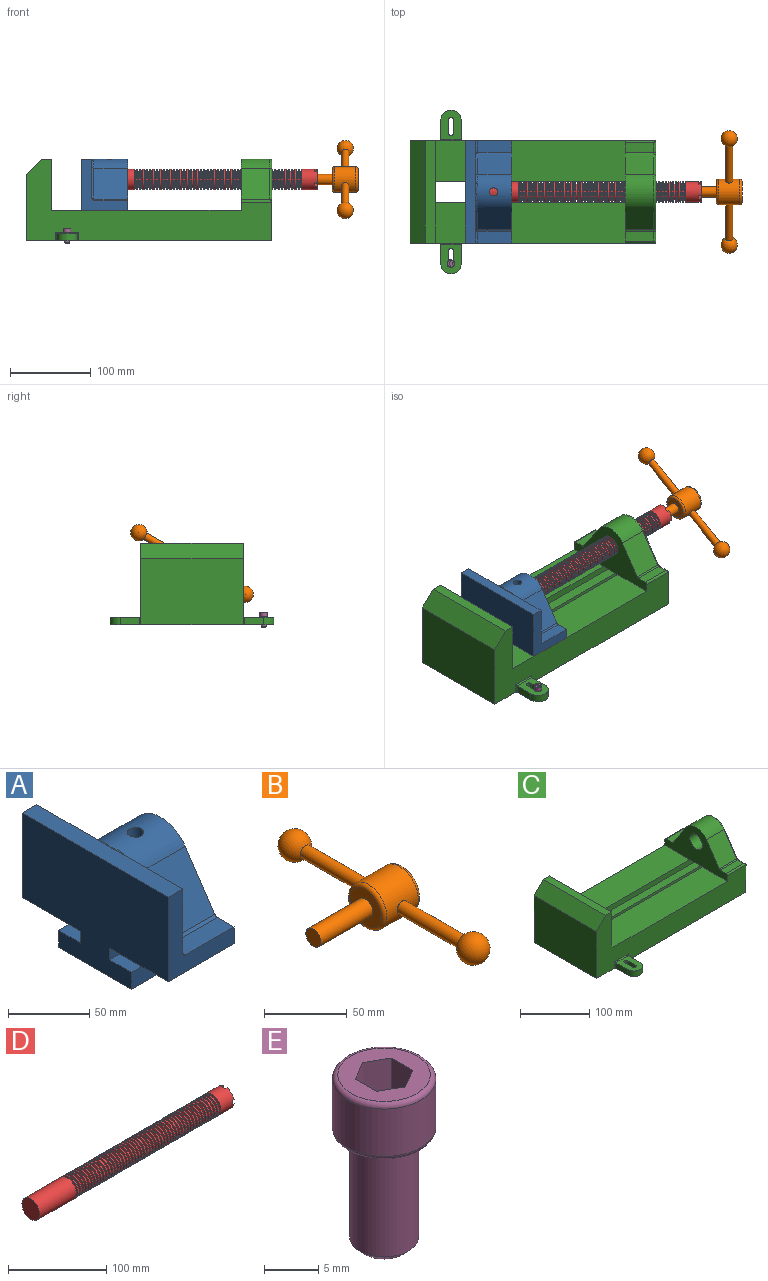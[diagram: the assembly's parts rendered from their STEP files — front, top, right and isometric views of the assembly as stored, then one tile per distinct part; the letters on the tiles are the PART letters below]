
ASSEMBLY  parts=5 mates=5
PART A: 36 faces, bbox 57.2x127x89 mm
  f0: plane 57.15x50.8mm, normal (0,0,-1), area 2903.2mm2, adj f6,f9,f10,f23
  f1: cylinder r=12.7mm len=44.45mm, axis (1,0,0), area 3464.3mm2, adj f6,f15,f16
  f2: plane 41.91x14.52mm, normal (0,0,1), area 608.5mm2, adj f6,f11,f24,f25
  f3: plane 51.86x48.26mm, normal (1,0,0), area 1495.7mm2, adj f8,f10,f31,f33,f35
  f4: plane 51.86x48.26mm, normal (1,0,0), area 1495.7mm2, adj f8,f11,f24,f28,f29
  f5: plane 57.15x50.8mm, normal (0,0,-1), area 2903.2mm2, adj f6,f9,f11,f22
  f6: plane 127x85.09mm, normal (1,0,0), area 5190.6mm2, adj f0,f1,f2,f5,f7,f10,f11,f12
  f7: plane 41.91x14.52mm, normal (0,0,1), area 608.5mm2, adj f6,f10,f30,f31
  f8: plane 127x12.7mm, normal (0,0,1), area 1612.9mm2, adj f3,f4,f9,f10,f11,f26,f34
  f9: plane 127x85.09mm, normal (-1,0,0), area 9096.8mm2, adj f0,f5,f8,f10,f11,f17,f18,f19
  f10: plane 63.5x57.15mm, normal (0,-1,0), area 1372.3mm2, adj f0,f3,f6,f7,f8,f9,f31
  f11: plane 63.5x57.15mm, normal (0,1,0), area 1372.3mm2, adj f2,f4,f5,f6,f8,f9,f24
  f12: plane 41.91x38.43mm, normal (0,-0.83,0.56), area 1939.2mm2, adj f6,f13,f30,f33
  f13: cylinder r=25.4mm len=44.45mm, axis (1,0,0), area 2026.5mm2, adj f6,f12,f14,f16,f26,f28,f34,f35
  f14: plane 41.91x38.43mm, normal (0,0.83,0.56), area 1939.2mm2, adj f6,f13,f25,f29
  f15: plane 25.4x25.4mm, normal (1,0,0), area 506.7mm2, adj f1
  f16: cylinder r=5.08mm len=13.76mm, axis (0,0,1), area 414mm2, adj f1,f13
  f17: plane 57.15x19.05mm, normal (0,0,1), area 1088.7mm2, adj f6,f9,f18,f23
  f18: plane 57.15x12.7mm, normal (0,-1,0), area 725.8mm2, adj f6,f9,f17,f19
  f19: plane 63.5x57.15mm, normal (0,0,-1), area 3629mm2, adj f6,f9,f18,f20
  f20: plane 57.15x12.7mm, normal (0,1,0), area 725.8mm2, adj f6,f9,f19,f21
  f21: plane 57.15x19.05mm, normal (0,0,1), area 1088.7mm2, adj f6,f9,f20,f22
  f22: plane 57.15x8.89mm, normal (0,1,0), area 508.1mm2, adj f5,f6,f9,f21
  f23: plane 57.15x8.89mm, normal (0,-1,0), area 508.1mm2, adj f0,f6,f9,f17
  f24: cylinder r=2.54mm len=14.52mm, axis (0,-1,0), area 57.9mm2, adj f2,f4,f11,f27
  f25: cylinder r=2.54mm len=41.91mm, axis (1,0,0), area 104.3mm2, adj f2,f6,f14,f27
  f26: bspline ~12.24x2.8mm, area 20.9mm2, adj f8,f13,f28
  f27: sphere r=2.54mm, area 6.3mm2, adj f24,f25,f29
  f28: torus R=27.94mm, axis (1,0,0), area 57.8mm2, adj f4,f13,f26,f29
  f29: cylinder r=2.54mm len=39.84mm, axis (0,-0.56,0.83), area 184.6mm2, adj f4,f14,f27,f28
  f30: cylinder r=2.54mm len=41.91mm, axis (1,0,0), area 104.3mm2, adj f6,f7,f12,f32
  f31: cylinder r=2.54mm len=14.52mm, axis (0,-1,0), area 57.9mm2, adj f3,f7,f10,f32
  f32: sphere r=2.54mm, area 6.3mm2, adj f30,f31,f33
  f33: cylinder r=2.54mm len=39.84mm, axis (0,-0.56,-0.83), area 184.6mm2, adj f3,f12,f32,f35
  f34: bspline ~12.24x2.8mm, area 20.9mm2, adj f8,f13,f35
  f35: torus R=27.94mm, axis (1,0,0), area 57.8mm2, adj f3,f13,f33,f34
PART B: 11 faces, bbox 76.2x172.7x34.4 mm
  f0: sphere r=10.16mm, area 1231.8mm2, adj f1
  f1: cylinder r=4.45mm len=51.82mm, axis (0,1,0), area 1438.5mm2, adj f0,f4
  f2: sphere r=10.16mm, area 1231.8mm2, adj f3
  f3: cylinder r=4.45mm len=51.82mm, axis (0,1,0), area 1438.5mm2, adj f2,f4
  f4: cylinder r=15.88mm len=31.75mm, axis (-1,0,0), area 2534.7mm2, adj f1,f3,f9,f10
  f5: cylinder r=6.35mm len=44.45mm, axis (-1,0,0), area 1773.5mm2, adj f6,f8
  f6: plane 12.7x12.7mm, normal (-1,0,0), area 126.7mm2, adj f5
  f7: plane 26.67x26.67mm, normal (1,0,0), area 558.6mm2, adj f10
  f8: plane 26.67x26.67mm, normal (-1,0,0), area 432mm2, adj f5,f9
  f9: torus R=13.33mm, axis (1,0,0), area 374.8mm2, adj f4,f8
  f10: torus R=13.33mm, axis (1,0,0), area 374.8mm2, adj f4,f7
PART C: 61 faces, bbox 304.8x203.2x103.7 mm
  f0: plane 304.8x101.6mm, normal (0,1,0), area 13520.3mm2, adj f3,f4,f5,f6,f7,f8,f9,f16
  f1: plane 304.8x101.6mm, normal (0,-1,0), area 13520.3mm2, adj f2,f3,f5,f6,f7,f8,f9,f16
  f2: plane 234.95x50.8mm, normal (0,0,1), area 11935.5mm2, adj f1,f5,f16,f26
  f3: plane 127x99.06mm, normal (1,0,0), area 7097.5mm2, adj f0,f1,f9,f14,f17,f18,f19,f20
  f4: plane 234.95x50.8mm, normal (0,0,1), area 11935.5mm2, adj f0,f5,f16,f27
  f5: plane 127x101.6mm, normal (1,0,0), area 9516.1mm2, adj f0,f1,f2,f4,f6,f9,f18,f19
  f6: plane 127x12.7mm, normal (0,0,1), area 1612.9mm2, adj f0,f1,f5,f7
  f7: plane 127x19.05mm, normal (-0.71,0,0.71), area 3421.5mm2, adj f0,f1,f6,f8
  f8: plane 127x82.55mm, normal (-1,0,0), area 10483.8mm2, adj f0,f1,f7,f9
  f9: plane 304.8x203.2mm, normal (0,0,-1), area 33298.3mm2, adj f0,f1,f3,f5,f8,f21,f22,f39
  f10: plane 35.56x11.98mm, normal (0,0,1), area 426mm2, adj f16,f28,f29,f30
  f11: plane 38.43x35.56mm, normal (0,0.83,0.56), area 1645.4mm2, adj f12,f16,f29,f32
  f12: cylinder r=25.4mm len=42.19mm, axis (1,0,0), area 1770.2mm2, adj f11,f13,f16,f33
  f13: plane 38.43x35.56mm, normal (0,-0.83,0.56), area 1645.4mm2, adj f12,f16,f34,f35
  f14: cylinder r=12.7mm len=38.1mm, axis (1,0,0), area 3040.2mm2, adj f3,f16
  f15: plane 35.56x11.98mm, normal (0,0,1), area 426mm2, adj f16,f34,f36,f38
  f16: plane 127x63.5mm, normal (-1,0,0), area 4155.5mm2, adj f0,f1,f2,f4,f10,f11,f12,f13
  f17: plane 38.1x25.4mm, normal (0,0,-1), area 967.7mm2, adj f3,f16,f26,f27
  f18: plane 273.05x19.05mm, normal (0,0,-1), area 5201.6mm2, adj f3,f5,f19,f26
  f19: plane 273.05x12.7mm, normal (0,1,0), area 3467.7mm2, adj f3,f5,f18,f20
  f20: plane 273.05x19.05mm, normal (0,0,1), area 5201.6mm2, adj f3,f5,f19,f21
  f21: plane 273.05x16.51mm, normal (0,1,0), area 4508.1mm2, adj f3,f5,f9,f20
  f22: plane 273.05x16.51mm, normal (0,-1,0), area 4508.1mm2, adj f3,f5,f9,f23
  f23: plane 273.05x19.05mm, normal (0,0,1), area 5201.6mm2, adj f3,f5,f22,f24
  f24: plane 273.05x12.7mm, normal (0,-1,0), area 3467.7mm2, adj f3,f5,f23,f25
  f25: plane 273.05x19.05mm, normal (0,0,-1), area 5201.6mm2, adj f3,f5,f24,f27
  f26: plane 273.05x8.89mm, normal (0,1,0), area 2427.4mm2, adj f2,f3,f5,f17,f18
  f27: plane 273.05x8.89mm, normal (0,-1,0), area 2427.4mm2, adj f3,f4,f5,f17,f25
  f28: cylinder r=2.54mm len=38.1mm, axis (1,0,0), area 148.3mm2, adj f0,f10,f16,f30
  f29: cylinder r=2.54mm len=35.56mm, axis (-1,0,0), area 88.5mm2, adj f10,f11,f16,f31
  f30: cylinder r=2.54mm len=14.52mm, axis (0,1,0), area 54.3mm2, adj f3,f10,f28,f31
  f31: torus R=5.08mm, axis (-1,0,0), area 13.5mm2, adj f3,f29,f30,f32
  f32: cylinder r=2.54mm len=39.84mm, axis (0,0.56,-0.83), area 184.6mm2, adj f3,f11,f31,f33
  f33: torus R=22.86mm, axis (-1,0,0), area 191.4mm2, adj f3,f12,f32,f35
  f34: cylinder r=2.54mm len=35.56mm, axis (-1,0,0), area 88.5mm2, adj f13,f15,f16,f37
  f35: cylinder r=2.54mm len=39.84mm, axis (0,0.56,0.83), area 184.6mm2, adj f3,f13,f33,f37
  f36: cylinder r=2.54mm len=38.1mm, axis (-1,0,0), area 148.3mm2, adj f1,f15,f16,f38
  f37: torus R=5.08mm, axis (-1,0,0), area 13.5mm2, adj f3,f34,f35,f38
  f38: cylinder r=2.54mm len=14.52mm, axis (0,1,0), area 54.3mm2, adj f3,f15,f36,f37
  f39: plane 23.88x9.53mm, normal (-1,0,0), area 227.4mm2, adj f9,f45,f46,f60
  f40: plane 23.88x9.53mm, normal (1,0,0), area 227.4mm2, adj f9,f45,f46,f58
  f41: cylinder r=3.3mm len=9.53mm, axis (0,0,-1), area 98.8mm2, adj f9,f42,f44,f46
  f42: plane 15.62x9.53mm, normal (-1,0,0), area 148.8mm2, adj f9,f41,f43,f46
  f43: cylinder r=3.3mm len=9.53mm, axis (0,0,-1), area 98.8mm2, adj f9,f42,f44,f46
  f44: plane 15.62x9.53mm, normal (1,0,0), area 148.8mm2, adj f9,f41,f43,f46
  f45: cylinder r=12.7mm len=25.4mm, axis (0,0,-1), area 380mm2, adj f9,f39,f40,f46
  f46: plane 36.58x25.4mm, normal (0,0,1), area 722.4mm2, adj f39,f40,f41,f42,f43,f44,f45,f59
  f47: plane 23.88x9.53mm, normal (-1,0,0), area 227.4mm2, adj f9,f53,f54,f56
  f48: plane 23.88x9.53mm, normal (1,0,0), area 227.4mm2, adj f9,f53,f54,f55
  f49: cylinder r=3.3mm len=9.53mm, axis (0,0,-1), area 98.8mm2, adj f9,f50,f52,f54
  f50: plane 15.62x9.53mm, normal (-1,0,0), area 148.8mm2, adj f9,f49,f51,f54
  f51: cylinder r=3.3mm len=9.53mm, axis (0,0,-1), area 98.8mm2, adj f9,f50,f52,f54
  f52: plane 15.62x9.53mm, normal (1,0,0), area 148.8mm2, adj f9,f49,f51,f54
  f53: cylinder r=12.7mm len=25.4mm, axis (0,0,-1), area 380mm2, adj f9,f47,f48,f54
  f54: plane 36.58x25.4mm, normal (0,0,1), area 722.4mm2, adj f47,f48,f49,f50,f51,f52,f53,f57
  f55: cylinder r=1.52mm len=11.05mm, axis (0,0,-1), area 24.1mm2, adj f0,f9,f48,f57
  f56: cylinder r=1.52mm len=11.05mm, axis (0,0,1), area 24.1mm2, adj f0,f9,f47,f57
  f57: cylinder r=1.52mm len=28.45mm, axis (1,0,0), area 63.5mm2, adj f0,f54,f55,f56
  f58: cylinder r=1.52mm len=11.05mm, axis (0,0,1), area 24.1mm2, adj f1,f9,f40,f59
  f59: cylinder r=1.52mm len=28.45mm, axis (-1,0,0), area 63.5mm2, adj f1,f46,f58,f60
  f60: cylinder r=1.52mm len=11.05mm, axis (0,0,-1), area 24.1mm2, adj f1,f9,f39,f59
PART D: 220 faces, bbox 279.4x25.4x25.4 mm
  f0: cylinder r=12.7mm len=25.4mm, axis (-1,0,0), area 1468.2mm2, adj f1,f2,f3,f5,f7,f208,f209,f210
  f1: plane 9.9x9.9mm, normal (1,0,0), area 62.3mm2, adj f0,f4,f213,f216
  f2: plane 9.9x9.9mm, normal (1,0,0), area 62.3mm2, adj f0,f4,f210,f218
  f3: plane 9.9x9.9mm, normal (1,0,0), area 62.3mm2, adj f0,f4,f209,f212
  f4: cylinder r=6.35mm len=25.4mm, axis (1,0,0), area 960.3mm2, adj f1,f2,f3,f5,f6,f208,f209,f210
  f5: plane 9.9x9.9mm, normal (1,0,0), area 62.3mm2, adj f0,f4,f215,f217
  f6: plane 12.7x12.7mm, normal (1,0,0), area 126.7mm2, adj f4
  f7: cone r=12.7mm half-angle=76deg, axis (1,0,0), area 188mm2, adj f0,f9
  f8: cone r=10.16mm half-angle=76deg, axis (-1,0,0), area 188mm2, adj f9,f10
  f9: cylinder r=10.16mm len=20.32mm, axis (1,0,0), area 81.1mm2, adj f7,f8
  f10: cylinder r=12.7mm len=25.4mm, axis (-1,0,0), area 131.7mm2, adj f8,f11
  f11: cone r=12.7mm half-angle=76deg, axis (1,0,0), area 188mm2, adj f10,f13
  f12: cone r=10.16mm half-angle=76deg, axis (-1,0,0), area 188mm2, adj f13,f14
  f13: cylinder r=10.16mm len=20.32mm, axis (1,0,0), area 81.1mm2, adj f11,f12
  f14: cylinder r=12.7mm len=25.4mm, axis (-1,0,0), area 131.7mm2, adj f12,f15
  f15: cone r=12.7mm half-angle=76deg, axis (1,0,0), area 188mm2, adj f14,f17
  f16: cone r=10.16mm half-angle=76deg, axis (-1,0,0), area 188mm2, adj f17,f18
  f17: cylinder r=10.16mm len=20.32mm, axis (1,0,0), area 81.1mm2, adj f15,f16
  f18: cylinder r=12.7mm len=25.4mm, axis (-1,0,0), area 131.7mm2, adj f16,f19
  f19: cone r=12.7mm half-angle=76deg, axis (1,0,0), area 188mm2, adj f18,f21
  f20: cone r=10.16mm half-angle=76deg, axis (-1,0,0), area 188mm2, adj f21,f22
  f21: cylinder r=10.16mm len=20.32mm, axis (1,0,0), area 81.1mm2, adj f19,f20
  f22: cylinder r=12.7mm len=25.4mm, axis (-1,0,0), area 131.7mm2, adj f20,f23
  f23: cone r=12.7mm half-angle=76deg, axis (1,0,0), area 188mm2, adj f22,f25
  f24: cone r=10.16mm half-angle=76deg, axis (-1,0,0), area 188mm2, adj f25,f26
  f25: cylinder r=10.16mm len=20.32mm, axis (1,0,0), area 81.1mm2, adj f23,f24
  f26: cylinder r=12.7mm len=25.4mm, axis (-1,0,0), area 131.7mm2, adj f24,f27
  f27: cone r=12.7mm half-angle=76deg, axis (1,0,0), area 188mm2, adj f26,f29
  f28: cone r=10.16mm half-angle=76deg, axis (-1,0,0), area 188mm2, adj f29,f30
  f29: cylinder r=10.16mm len=20.32mm, axis (1,0,0), area 81.1mm2, adj f27,f28
  f30: cylinder r=12.7mm len=25.4mm, axis (-1,0,0), area 131.7mm2, adj f28,f31
  f31: cone r=12.7mm half-angle=76deg, axis (1,0,0), area 188mm2, adj f30,f33
  f32: cone r=10.16mm half-angle=76deg, axis (-1,0,0), area 188mm2, adj f33,f34
  f33: cylinder r=10.16mm len=20.32mm, axis (1,0,0), area 81.1mm2, adj f31,f32
  f34: cylinder r=12.7mm len=25.4mm, axis (-1,0,0), area 131.7mm2, adj f32,f35
  f35: cone r=12.7mm half-angle=76deg, axis (1,0,0), area 188mm2, adj f34,f37
  f36: cone r=10.16mm half-angle=76deg, axis (-1,0,0), area 188mm2, adj f37,f38
  f37: cylinder r=10.16mm len=20.32mm, axis (1,0,0), area 81.1mm2, adj f35,f36
  f38: cylinder r=12.7mm len=25.4mm, axis (-1,0,0), area 131.7mm2, adj f36,f39
  f39: cone r=12.7mm half-angle=76deg, axis (1,0,0), area 188mm2, adj f38,f41
  f40: cone r=10.16mm half-angle=76deg, axis (-1,0,0), area 188mm2, adj f41,f42
  f41: cylinder r=10.16mm len=20.32mm, axis (1,0,0), area 81.1mm2, adj f39,f40
  f42: cylinder r=12.7mm len=25.4mm, axis (-1,0,0), area 131.7mm2, adj f40,f43
  f43: cone r=12.7mm half-angle=76deg, axis (1,0,0), area 188mm2, adj f42,f45
  f44: cone r=10.16mm half-angle=76deg, axis (-1,0,0), area 188mm2, adj f45,f46
  f45: cylinder r=10.16mm len=20.32mm, axis (1,0,0), area 81.1mm2, adj f43,f44
  f46: cylinder r=12.7mm len=25.4mm, axis (-1,0,0), area 131.7mm2, adj f44,f47
  f47: cone r=12.7mm half-angle=76deg, axis (1,0,0), area 188mm2, adj f46,f49
  f48: cone r=10.16mm half-angle=76deg, axis (-1,0,0), area 188mm2, adj f49,f50
  f49: cylinder r=10.16mm len=20.32mm, axis (1,0,0), area 81.1mm2, adj f47,f48
  f50: cylinder r=12.7mm len=25.4mm, axis (-1,0,0), area 131.7mm2, adj f48,f51
  f51: cone r=12.7mm half-angle=76deg, axis (1,0,0), area 188mm2, adj f50,f53
  f52: cone r=10.16mm half-angle=76deg, axis (-1,0,0), area 188mm2, adj f53,f54
  f53: cylinder r=10.16mm len=20.32mm, axis (1,0,0), area 81.1mm2, adj f51,f52
  f54: cylinder r=12.7mm len=25.4mm, axis (-1,0,0), area 131.7mm2, adj f52,f55
  f55: cone r=12.7mm half-angle=76deg, axis (1,0,0), area 188mm2, adj f54,f57
  f56: cone r=10.16mm half-angle=76deg, axis (-1,0,0), area 188mm2, adj f57,f58
  f57: cylinder r=10.16mm len=20.32mm, axis (1,0,0), area 81.1mm2, adj f55,f56
  f58: cylinder r=12.7mm len=25.4mm, axis (-1,0,0), area 131.7mm2, adj f56,f59
  f59: cone r=12.7mm half-angle=76deg, axis (1,0,0), area 188mm2, adj f58,f61
  f60: cone r=10.16mm half-angle=76deg, axis (-1,0,0), area 188mm2, adj f61,f62
  f61: cylinder r=10.16mm len=20.32mm, axis (1,0,0), area 81.1mm2, adj f59,f60
  f62: cylinder r=12.7mm len=25.4mm, axis (-1,0,0), area 131.7mm2, adj f60,f63
  f63: cone r=12.7mm half-angle=76deg, axis (1,0,0), area 188mm2, adj f62,f65
  f64: cone r=10.16mm half-angle=76deg, axis (-1,0,0), area 188mm2, adj f65,f66
  f65: cylinder r=10.16mm len=20.32mm, axis (1,0,0), area 81.1mm2, adj f63,f64
  f66: cylinder r=12.7mm len=25.4mm, axis (-1,0,0), area 131.7mm2, adj f64,f67
  f67: cone r=12.7mm half-angle=76deg, axis (1,0,0), area 188mm2, adj f66,f69
  f68: cone r=10.16mm half-angle=76deg, axis (-1,0,0), area 188mm2, adj f69,f70
  f69: cylinder r=10.16mm len=20.32mm, axis (1,0,0), area 81.1mm2, adj f67,f68
  f70: cylinder r=12.7mm len=25.4mm, axis (-1,0,0), area 131.7mm2, adj f68,f71
  f71: cone r=12.7mm half-angle=76deg, axis (1,0,0), area 188mm2, adj f70,f73
  f72: cone r=10.16mm half-angle=76deg, axis (-1,0,0), area 188mm2, adj f73,f74
  f73: cylinder r=10.16mm len=20.32mm, axis (1,0,0), area 81.1mm2, adj f71,f72
  f74: cylinder r=12.7mm len=25.4mm, axis (-1,0,0), area 131.7mm2, adj f72,f75
  f75: cone r=12.7mm half-angle=76deg, axis (1,0,0), area 188mm2, adj f74,f77
  f76: cone r=10.16mm half-angle=76deg, axis (-1,0,0), area 188mm2, adj f77,f78
  f77: cylinder r=10.16mm len=20.32mm, axis (1,0,0), area 81.1mm2, adj f75,f76
  f78: cylinder r=12.7mm len=25.4mm, axis (-1,0,0), area 131.7mm2, adj f76,f79
  f79: cone r=12.7mm half-angle=76deg, axis (1,0,0), area 188mm2, adj f78,f81
  f80: cone r=10.16mm half-angle=76deg, axis (-1,0,0), area 188mm2, adj f81,f82
  f81: cylinder r=10.16mm len=20.32mm, axis (1,0,0), area 81.1mm2, adj f79,f80
  f82: cylinder r=12.7mm len=25.4mm, axis (-1,0,0), area 131.7mm2, adj f80,f83
  f83: cone r=12.7mm half-angle=76deg, axis (1,0,0), area 188mm2, adj f82,f85
  f84: cone r=10.16mm half-angle=76deg, axis (-1,0,0), area 188mm2, adj f85,f86
  f85: cylinder r=10.16mm len=20.32mm, axis (1,0,0), area 81.1mm2, adj f83,f84
  f86: cylinder r=12.7mm len=25.4mm, axis (-1,0,0), area 131.7mm2, adj f84,f87
  f87: cone r=12.7mm half-angle=76deg, axis (1,0,0), area 188mm2, adj f86,f89
  f88: cone r=10.16mm half-angle=76deg, axis (-1,0,0), area 188mm2, adj f89,f90
  f89: cylinder r=10.16mm len=20.32mm, axis (1,0,0), area 81.1mm2, adj f87,f88
  f90: cylinder r=12.7mm len=25.4mm, axis (-1,0,0), area 131.7mm2, adj f88,f91
  f91: cone r=12.7mm half-angle=76deg, axis (1,0,0), area 188mm2, adj f90,f93
  f92: cone r=10.16mm half-angle=76deg, axis (-1,0,0), area 188mm2, adj f93,f94
  f93: cylinder r=10.16mm len=20.32mm, axis (1,0,0), area 81.1mm2, adj f91,f92
  f94: cylinder r=12.7mm len=25.4mm, axis (-1,0,0), area 131.7mm2, adj f92,f95
  f95: cone r=12.7mm half-angle=76deg, axis (1,0,0), area 188mm2, adj f94,f97
  f96: cone r=10.16mm half-angle=76deg, axis (-1,0,0), area 188mm2, adj f97,f98
  f97: cylinder r=10.16mm len=20.32mm, axis (1,0,0), area 81.1mm2, adj f95,f96
  f98: cylinder r=12.7mm len=25.4mm, axis (-1,0,0), area 131.7mm2, adj f96,f99
  f99: cone r=12.7mm half-angle=76deg, axis (1,0,0), area 188mm2, adj f98,f101
  f100: cone r=10.16mm half-angle=76deg, axis (-1,0,0), area 188mm2, adj f101,f102
  f101: cylinder r=10.16mm len=20.32mm, axis (1,0,0), area 81.1mm2, adj f99,f100
  f102: cylinder r=12.7mm len=25.4mm, axis (-1,0,0), area 131.7mm2, adj f100,f103
  f103: cone r=12.7mm half-angle=76deg, axis (1,0,0), area 188mm2, adj f102,f105
  f104: cone r=10.16mm half-angle=76deg, axis (-1,0,0), area 188mm2, adj f105,f106
  f105: cylinder r=10.16mm len=20.32mm, axis (1,0,0), area 81.1mm2, adj f103,f104
  f106: cylinder r=12.7mm len=25.4mm, axis (-1,0,0), area 131.7mm2, adj f104,f107
  f107: cone r=12.7mm half-angle=76deg, axis (1,0,0), area 188mm2, adj f106,f109
  f108: cone r=10.16mm half-angle=76deg, axis (-1,0,0), area 188mm2, adj f109,f110
  f109: cylinder r=10.16mm len=20.32mm, axis (1,0,0), area 81.1mm2, adj f107,f108
  f110: cylinder r=12.7mm len=25.4mm, axis (-1,0,0), area 131.7mm2, adj f108,f111
  f111: cone r=12.7mm half-angle=76deg, axis (1,0,0), area 188mm2, adj f110,f113
  f112: cone r=10.16mm half-angle=76deg, axis (-1,0,0), area 188mm2, adj f113,f114
  f113: cylinder r=10.16mm len=20.32mm, axis (1,0,0), area 81.1mm2, adj f111,f112
  f114: cylinder r=12.7mm len=25.4mm, axis (-1,0,0), area 131.7mm2, adj f112,f115
  f115: cone r=12.7mm half-angle=76deg, axis (1,0,0), area 188mm2, adj f114,f117
  f116: cone r=10.16mm half-angle=76deg, axis (-1,0,0), area 188mm2, adj f117,f118
  f117: cylinder r=10.16mm len=20.32mm, axis (1,0,0), area 81.1mm2, adj f115,f116
  f118: cylinder r=12.7mm len=25.4mm, axis (-1,0,0), area 131.7mm2, adj f116,f119
  f119: cone r=12.7mm half-angle=76deg, axis (1,0,0), area 188mm2, adj f118,f121
  f120: cone r=10.16mm half-angle=76deg, axis (-1,0,0), area 188mm2, adj f121,f122
  f121: cylinder r=10.16mm len=20.32mm, axis (1,0,0), area 81.1mm2, adj f119,f120
  f122: cylinder r=12.7mm len=25.4mm, axis (-1,0,0), area 131.7mm2, adj f120,f123
  f123: cone r=12.7mm half-angle=76deg, axis (1,0,0), area 188mm2, adj f122,f125
  f124: cone r=10.16mm half-angle=76deg, axis (-1,0,0), area 188mm2, adj f125,f126
  f125: cylinder r=10.16mm len=20.32mm, axis (1,0,0), area 81.1mm2, adj f123,f124
  f126: cylinder r=12.7mm len=25.4mm, axis (-1,0,0), area 131.7mm2, adj f124,f127
  f127: cone r=12.7mm half-angle=76deg, axis (1,0,0), area 188mm2, adj f126,f129
  f128: cone r=10.16mm half-angle=76deg, axis (-1,0,0), area 188mm2, adj f129,f130
  f129: cylinder r=10.16mm len=20.32mm, axis (1,0,0), area 81.1mm2, adj f127,f128
  f130: cylinder r=12.7mm len=25.4mm, axis (-1,0,0), area 131.7mm2, adj f128,f131
  f131: cone r=12.7mm half-angle=76deg, axis (1,0,0), area 188mm2, adj f130,f133
  f132: cone r=10.16mm half-angle=76deg, axis (-1,0,0), area 188mm2, adj f133,f134
  f133: cylinder r=10.16mm len=20.32mm, axis (1,0,0), area 81.1mm2, adj f131,f132
  f134: cylinder r=12.7mm len=25.4mm, axis (-1,0,0), area 131.7mm2, adj f132,f135
  f135: cone r=12.7mm half-angle=76deg, axis (1,0,0), area 188mm2, adj f134,f137
  f136: cone r=10.16mm half-angle=76deg, axis (-1,0,0), area 188mm2, adj f137,f138
  f137: cylinder r=10.16mm len=20.32mm, axis (1,0,0), area 81.1mm2, adj f135,f136
  f138: cylinder r=12.7mm len=25.4mm, axis (-1,0,0), area 131.7mm2, adj f136,f139
  f139: cone r=12.7mm half-angle=76deg, axis (1,0,0), area 188mm2, adj f138,f141
  f140: cone r=10.16mm half-angle=76deg, axis (-1,0,0), area 188mm2, adj f141,f142
  f141: cylinder r=10.16mm len=20.32mm, axis (1,0,0), area 81.1mm2, adj f139,f140
  f142: cylinder r=12.7mm len=25.4mm, axis (-1,0,0), area 131.7mm2, adj f140,f143
  f143: cone r=12.7mm half-angle=76deg, axis (1,0,0), area 188mm2, adj f142,f145
  f144: cone r=10.16mm half-angle=76deg, axis (-1,0,0), area 188mm2, adj f145,f146
  f145: cylinder r=10.16mm len=20.32mm, axis (1,0,0), area 81.1mm2, adj f143,f144
  f146: cylinder r=12.7mm len=25.4mm, axis (-1,0,0), area 131.7mm2, adj f144,f147
  f147: cone r=12.7mm half-angle=76deg, axis (1,0,0), area 188mm2, adj f146,f149
  f148: cone r=10.16mm half-angle=76deg, axis (-1,0,0), area 188mm2, adj f149,f150
  f149: cylinder r=10.16mm len=20.32mm, axis (1,0,0), area 81.1mm2, adj f147,f148
  f150: cylinder r=12.7mm len=25.4mm, axis (-1,0,0), area 131.7mm2, adj f148,f151
  f151: cone r=12.7mm half-angle=76deg, axis (1,0,0), area 188mm2, adj f150,f153
  f152: cone r=10.16mm half-angle=76deg, axis (-1,0,0), area 188mm2, adj f153,f154
  f153: cylinder r=10.16mm len=20.32mm, axis (1,0,0), area 81.1mm2, adj f151,f152
  f154: cylinder r=12.7mm len=25.4mm, axis (-1,0,0), area 131.7mm2, adj f152,f155
  f155: cone r=12.7mm half-angle=76deg, axis (1,0,0), area 188mm2, adj f154,f157
  f156: cone r=10.16mm half-angle=76deg, axis (-1,0,0), area 188mm2, adj f157,f158
  f157: cylinder r=10.16mm len=20.32mm, axis (1,0,0), area 81.1mm2, adj f155,f156
  f158: cylinder r=12.7mm len=25.4mm, axis (-1,0,0), area 131.7mm2, adj f156,f159
  f159: cone r=12.7mm half-angle=76deg, axis (1,0,0), area 188mm2, adj f158,f161
  f160: cone r=10.16mm half-angle=76deg, axis (-1,0,0), area 188mm2, adj f161,f162
  f161: cylinder r=10.16mm len=20.32mm, axis (1,0,0), area 81.1mm2, adj f159,f160
  f162: cylinder r=12.7mm len=25.4mm, axis (-1,0,0), area 131.7mm2, adj f160,f163
  f163: cone r=12.7mm half-angle=76deg, axis (1,0,0), area 188mm2, adj f162,f165
  f164: cone r=10.16mm half-angle=76deg, axis (-1,0,0), area 188mm2, adj f165,f166
  f165: cylinder r=10.16mm len=20.32mm, axis (1,0,0), area 81.1mm2, adj f163,f164
  f166: cylinder r=12.7mm len=25.4mm, axis (-1,0,0), area 131.7mm2, adj f164,f167
  f167: cone r=12.7mm half-angle=76deg, axis (1,0,0), area 188mm2, adj f166,f169
  f168: cone r=10.16mm half-angle=76deg, axis (-1,0,0), area 188mm2, adj f169,f170
  f169: cylinder r=10.16mm len=20.32mm, axis (1,0,0), area 81.1mm2, adj f167,f168
  f170: cylinder r=12.7mm len=25.4mm, axis (-1,0,0), area 131.7mm2, adj f168,f171
  f171: cone r=12.7mm half-angle=76deg, axis (1,0,0), area 188mm2, adj f170,f173
  f172: cone r=10.16mm half-angle=76deg, axis (-1,0,0), area 188mm2, adj f173,f174
  f173: cylinder r=10.16mm len=20.32mm, axis (1,0,0), area 81.1mm2, adj f171,f172
  f174: cylinder r=12.7mm len=25.4mm, axis (-1,0,0), area 131.7mm2, adj f172,f175
  f175: cone r=12.7mm half-angle=76deg, axis (1,0,0), area 188mm2, adj f174,f177
  f176: cone r=10.16mm half-angle=76deg, axis (-1,0,0), area 188mm2, adj f177,f178
  f177: cylinder r=10.16mm len=20.32mm, axis (1,0,0), area 81.1mm2, adj f175,f176
  f178: cylinder r=12.7mm len=25.4mm, axis (-1,0,0), area 131.7mm2, adj f176,f179
  f179: cone r=12.7mm half-angle=76deg, axis (1,0,0), area 188mm2, adj f178,f181
  f180: cone r=10.16mm half-angle=76deg, axis (-1,0,0), area 188mm2, adj f181,f182
  f181: cylinder r=10.16mm len=20.32mm, axis (1,0,0), area 81.1mm2, adj f179,f180
  f182: cylinder r=12.7mm len=25.4mm, axis (-1,0,0), area 131.7mm2, adj f180,f183
  f183: cone r=12.7mm half-angle=76deg, axis (1,0,0), area 188mm2, adj f182,f185
  f184: cone r=10.16mm half-angle=76deg, axis (-1,0,0), area 188mm2, adj f185,f186
  f185: cylinder r=10.16mm len=20.32mm, axis (1,0,0), area 81.1mm2, adj f183,f184
  f186: cylinder r=12.7mm len=25.4mm, axis (-1,0,0), area 131.7mm2, adj f184,f187
  f187: cone r=12.7mm half-angle=76deg, axis (1,0,0), area 188mm2, adj f186,f189
  f188: cone r=10.16mm half-angle=76deg, axis (-1,0,0), area 188mm2, adj f189,f190
  f189: cylinder r=10.16mm len=20.32mm, axis (1,0,0), area 81.1mm2, adj f187,f188
  f190: cylinder r=12.7mm len=25.4mm, axis (-1,0,0), area 131.7mm2, adj f188,f191
  f191: cone r=12.7mm half-angle=76deg, axis (1,0,0), area 188mm2, adj f190,f193
  f192: cone r=10.16mm half-angle=76deg, axis (-1,0,0), area 188mm2, adj f193,f194
  f193: cylinder r=10.16mm len=20.32mm, axis (1,0,0), area 81.1mm2, adj f191,f192
  f194: cylinder r=12.7mm len=25.4mm, axis (-1,0,0), area 131.7mm2, adj f192,f195
  f195: cone r=12.7mm half-angle=76deg, axis (1,0,0), area 188mm2, adj f194,f197
  f196: cone r=10.16mm half-angle=76deg, axis (-1,0,0), area 188mm2, adj f197,f198
  f197: cylinder r=10.16mm len=20.32mm, axis (1,0,0), area 81.1mm2, adj f195,f196
  f198: cylinder r=12.7mm len=25.4mm, axis (-1,0,0), area 131.7mm2, adj f196,f199
  f199: cone r=12.7mm half-angle=76deg, axis (1,0,0), area 188mm2, adj f198,f201
  f200: cone r=10.16mm half-angle=76deg, axis (-1,0,0), area 188mm2, adj f201,f202
  f201: cylinder r=10.16mm len=20.32mm, axis (1,0,0), area 81.1mm2, adj f199,f200
  f202: cylinder r=12.7mm len=25.4mm, axis (-1,0,0), area 131.7mm2, adj f200,f203
  f203: cone r=12.7mm half-angle=76deg, axis (1,0,0), area 188mm2, adj f202,f205
  f204: cone r=10.16mm half-angle=76deg, axis (-1,0,0), area 188mm2, adj f205,f207
  f205: cylinder r=10.16mm len=20.32mm, axis (1,0,0), area 81.1mm2, adj f203,f204
  f206: plane 25.4x25.4mm, normal (-1,0,0), area 506.7mm2, adj f207
  f207: cylinder r=12.7mm len=52.45mm, axis (-1,0,0), area 4185.4mm2, adj f204,f206
  f208: plane 6.88x5.08mm, normal (1,0,0), area 32.7mm2, adj f0,f4,f209,f210
  f209: plane 6.62x2.54mm, normal (0,-1,0), area 16.8mm2, adj f0,f3,f4,f208
  f210: plane 6.62x2.54mm, normal (0,1,0), area 16.8mm2, adj f0,f2,f4,f208
  f211: plane 6.88x5.08mm, normal (1,0,0), area 32.7mm2, adj f0,f4,f212,f213
  f212: plane 6.62x2.54mm, normal (0,0,1), area 16.8mm2, adj f0,f3,f4,f211
  f213: plane 6.62x2.54mm, normal (0,0,-1), area 16.8mm2, adj f0,f1,f4,f211
  f214: plane 6.88x5.08mm, normal (1,0,0), area 32.7mm2, adj f0,f4,f215,f216
  f215: plane 6.62x2.54mm, normal (0,1,0), area 16.8mm2, adj f0,f4,f5,f214
  f216: plane 6.62x2.54mm, normal (0,-1,0), area 16.8mm2, adj f0,f1,f4,f214
  f217: plane 6.62x2.54mm, normal (0,0,-1), area 16.8mm2, adj f0,f4,f5,f219
  f218: plane 6.62x2.54mm, normal (0,0,1), area 16.8mm2, adj f0,f2,f4,f219
  f219: plane 6.88x5.08mm, normal (1,0,0), area 32.7mm2, adj f0,f4,f217,f218
PART E: 15 faces, bbox 10.3x10.3x19.1 mm
  f0: plane 8.51x8.51mm, normal (0,0,1), area 37.2mm2, adj f5,f6,f7,f8,f9,f10,f14
  f1: cylinder r=3.17mm len=11.94mm, axis (0,0,1), area 238.2mm2, adj f4,f12
  f2: plane 4.83x4.83mm, normal (0,0,-1), area 18.3mm2, adj f12
  f3: cylinder r=4.76mm len=9.53mm, axis (0,0,-1), area 159.6mm2, adj f13,f14
  f4: plane 8.51x8.51mm, normal (0,0,-1), area 25.2mm2, adj f1,f13
  f5: plane 4.83x2.38mm, normal (-0.5,-0.87,0), area 13.3mm2, adj f0,f6,f10,f11
  f6: plane 4.83x2.38mm, normal (0.5,-0.87,0), area 13.3mm2, adj f0,f5,f7,f11
  f7: plane 4.83x2.75mm, normal (1,0,0), area 13.3mm2, adj f0,f6,f8,f11
  f8: plane 4.83x2.38mm, normal (0.5,0.87,0), area 13.3mm2, adj f0,f7,f9,f11
  f9: plane 4.83x2.38mm, normal (-0.5,0.87,0), area 13.3mm2, adj f0,f8,f10,f11
  f10: plane 4.83x2.75mm, normal (-1,0,0), area 13.3mm2, adj f0,f5,f9,f11
  f11: plane 5.5x4.76mm, normal (0,0,1), area 19.6mm2, adj f5,f6,f7,f8,f9,f10
  f12: cone r=3.17mm half-angle=45deg, axis (0,0,1), area 18.9mm2, adj f1,f2
  f13: torus R=4.25mm, axis (0,0,1), area 23mm2, adj f3,f4
  f14: torus R=4.25mm, axis (0,0,1), area 23mm2, adj f0,f3
PLACE A t=(176.31,58.59,0.41)mm
PLACE B rot(axis=(-1,0,0),149.8deg) t=(176.31,20.29,142.49)mm
PLACE C t=(139.27,58.59,0.41)mm fixed
PLACE D rot(axis=(-1,0,0),149.8deg) t=(176.31,20.29,142.49)mm
PLACE E t=(-114.73,-30.31,9.94)mm
MATE revolute D.f7 <-> A.f28  axis (-1,0,0) through (-84.04,58.59,76.61)mm
MATE fastened B.f5 <-> D.f4  axis (-1,0,0) through (169.96,58.59,76.61)mm
MATE slider C.f12 <-> A.f28  axis (-1,0,0) through (101.17,58.59,76.61)mm
MATE pin_slot C.f41 <-> E.f1  axis (0,0,1) through (-114.73,-30.31,9.94)mm
MATE cylindrical D.f7 <-> C.f12  axis (-1,0,0) through (-84.04,58.59,76.61)mm
